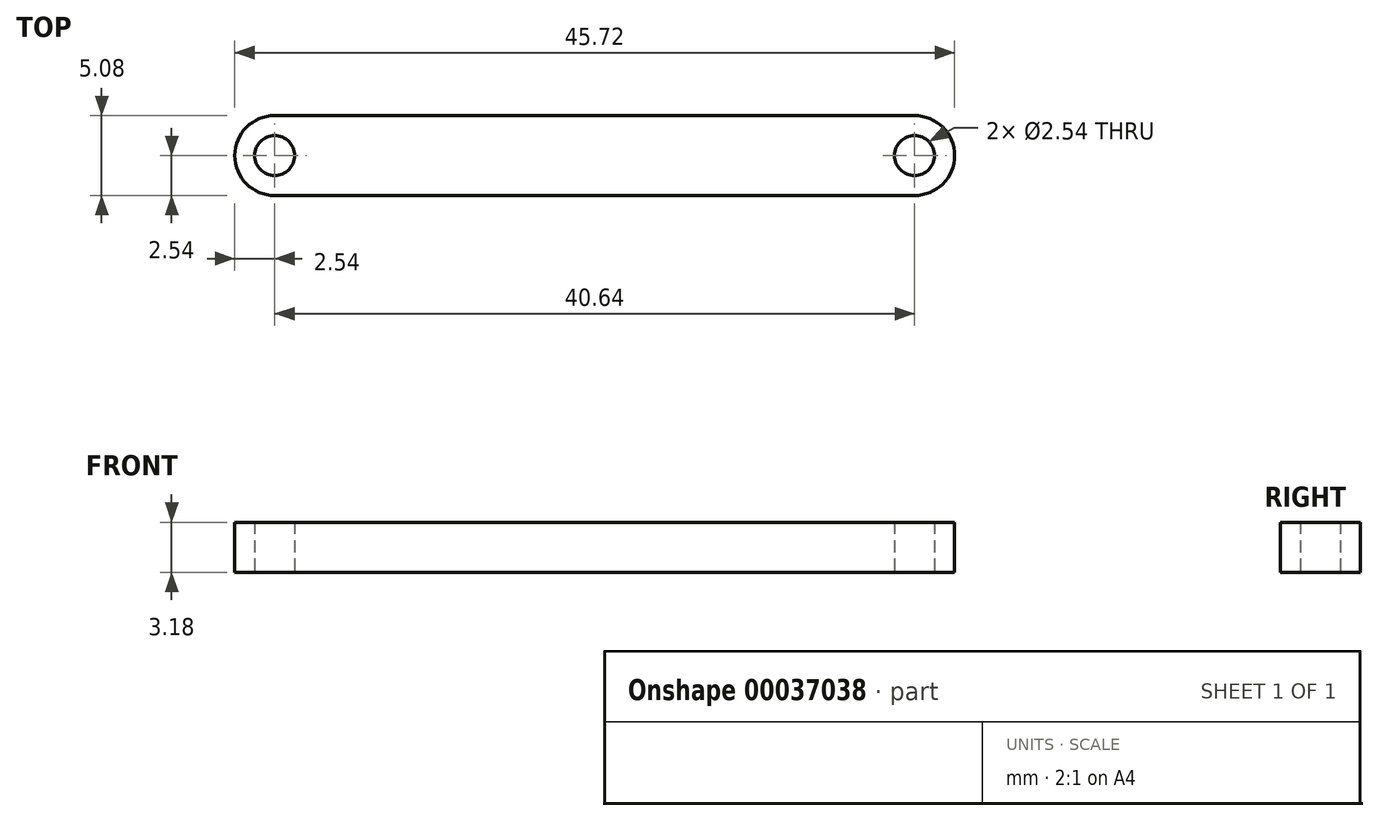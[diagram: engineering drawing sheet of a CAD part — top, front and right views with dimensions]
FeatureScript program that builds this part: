
annotation { "Feature Type Name" : "Feature", "Feature Type Description" : "" }
export const myFeature = defineFeature(function(context is Context, id is Id, definition is map)
    precondition{}
    {
        {
            var Q0;
            Q0=qCreatedBy(makeId("Top.planeOp"),FACE);
            var sketch = newSketch(context, id + "F0", { "sketchPlane" : qUnion([Q0])});
            skLineSegment(sketch, "E0.rect.bottom", {"start": v(20.32, 2.54) * mm, "end": v(-20.32, 2.54) * mm});
            skLineSegment(sketch, "E0.rect.top", {"start": v(20.32, -2.54) * mm, "end": v(-20.32, -2.54) * mm});
            skLineSegment(sketch, "E0.rect.left", {"start": v(20.32, 2.54) * mm, "end": v(20.32, -2.54) * mm});
            skLineSegment(sketch, "E0.rect.right", {"start": v(-20.32, 2.54) * mm, "end": v(-20.32, -2.54) * mm});
            skPoint(sketch, "E0.rect.middle", {"position": v(0, 0) * mm});
            skArc(sketch, "E1", {"start": v(20.32, -2.54) * mm, "mid": v(22.86, 0) * mm, "end": v(20.32, 2.54) * mm});
            skArc(sketch, "E2", {"start": v(-20.32, 2.54) * mm, "mid": v(-22.86, 0) * mm, "end": v(-20.32, -2.54) * mm});
            skCircle(sketch, "E3", {"center": v(-20.32, 0) * mm, "radius": 1.27 * mm});
            skCircle(sketch, "E4", {"center": v(20.32, 0) * mm, "radius": 1.27 * mm});
            skSolve(sketch);
        }
        {
            var Q0;
            Q0=qSketchRegion(id+"F0",true);
            extrude(context, id + "F1", {"entities" : qUnion([Q0]), "depth" : 3.17 * mm});
        }
    });
